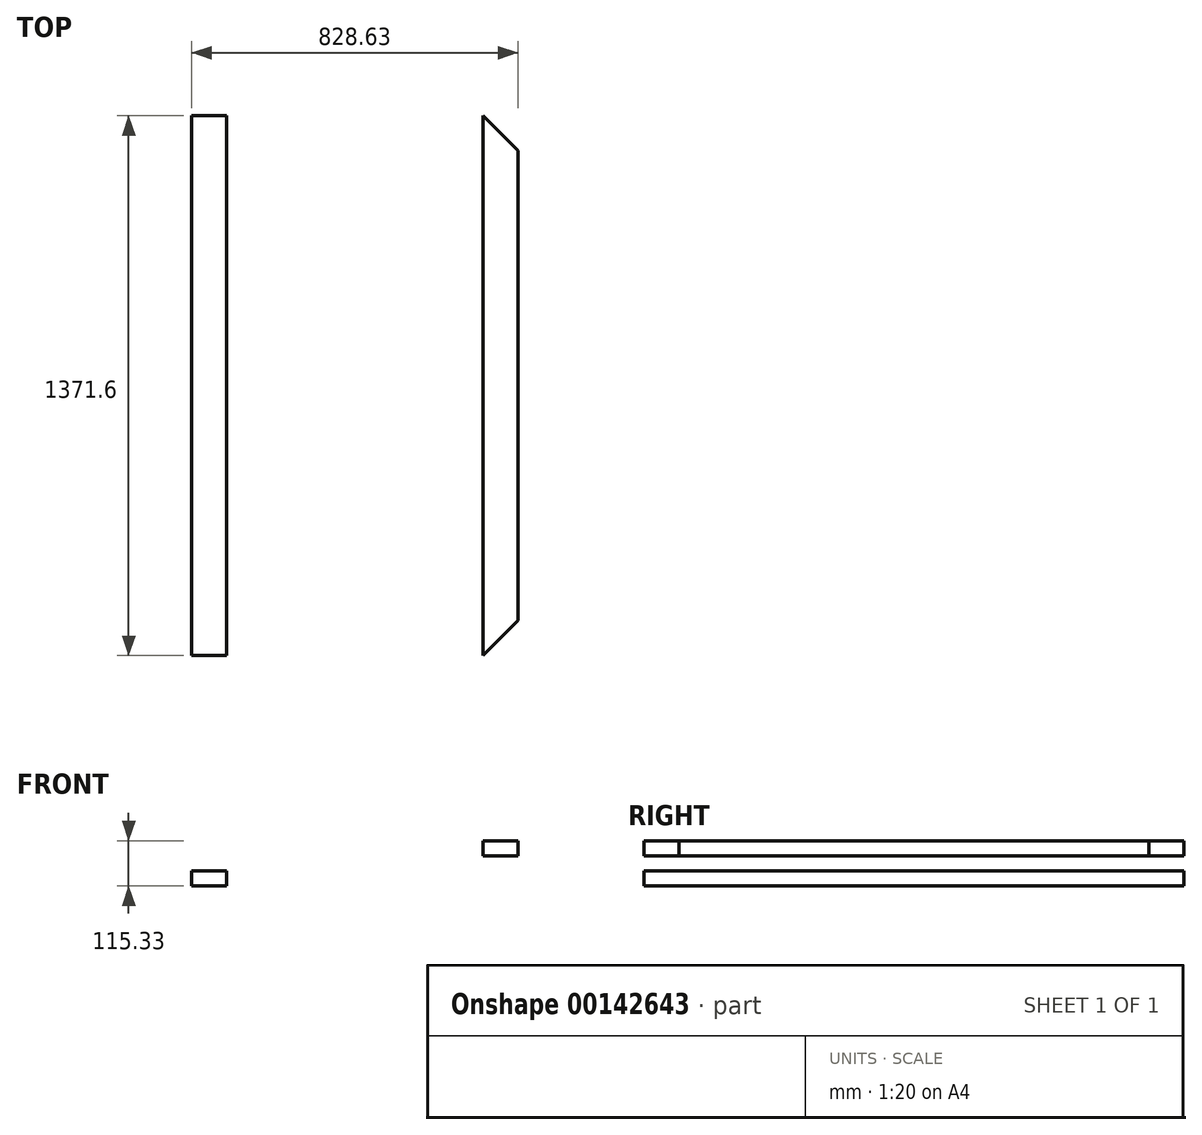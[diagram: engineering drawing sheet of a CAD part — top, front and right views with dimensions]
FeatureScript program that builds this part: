
annotation { "Feature Type Name" : "Feature", "Feature Type Description" : "" }
export const myFeature = defineFeature(function(context is Context, id is Id, definition is map)
    precondition{}
    {
        {
            var Q0;
            Q0=qCreatedBy(makeId("Front.planeOp"),FACE);
            var sketch = newSketch(context, id + "F0", { "sketchPlane" : qUnion([Q0])});
            skLineSegment(sketch, "E0.bottom", {"start": v(0, 0) * mm, "end": v(88.9, 0) * mm});
            skLineSegment(sketch, "E0.top", {"start": v(0, 38.1) * mm, "end": v(88.9, 38.1) * mm});
            skLineSegment(sketch, "E0.left", {"start": v(0, 0) * mm, "end": v(0, 38.1) * mm});
            skLineSegment(sketch, "E0.right", {"start": v(88.9, 0) * mm, "end": v(88.9, 38.1) * mm});
            skSolve(sketch);
        }
        {
            var Q0;
            Q0 = qSketchRegion(id + "F0", true);
            extrude(context, id + "F1", {"entities" : qUnion([Q0]), "depth" : 1371.6 * mm});
        }
        {
            var Q0;
            Q0=makeQuery(id+"F1.opExtrude","SWEPT_FACE",FACE,{"disambiguationData":[OSD([sQuery(id+"F0.wireOp",EDGE,"E0.top")])]});
            var sketch = newSketch(context, id + "F2", { "sketchPlane" : qUnion([Q0])});
            skLineSegment(sketch, "E1", {"start": v(0, -1371.6) * mm, "end": v(88.9, -1282.7) * mm});
            skLineSegment(sketch, "E2", {"start": v(88.9, -1282.7) * mm, "end": v(88.9, -1371.6) * mm});
            skLineSegment(sketch, "E3", {"start": v(88.9, -1371.6) * mm, "end": v(0, -1371.6) * mm});
            skLineSegment(sketch, "E4", {"start": v(88.9, -88.9) * mm, "end": v(0, 0) * mm});
            skLineSegment(sketch, "E5", {"start": v(0, 0) * mm, "end": v(88.9, 0) * mm});
            skLineSegment(sketch, "E6", {"start": v(88.9, 0) * mm, "end": v(88.9, -88.9) * mm});
            skSolve(sketch);
        }
        {
            var Q0;
            Q0 = qSketchRegion(id + "F2", true);
            extrude(context, id + "F3", {"entities" : qUnion([Q0]), "operationType" : NewBodyOperationType.REMOVE, "endBound" : BoundingType.UP_TO_NEXT, "oppositeDirection" : true, "depth" : 25.4 * mm});
        }
        {
            var Q0;
            Q0=qCreatedBy(makeId("Front.planeOp"),FACE);
            var sketch = newSketch(context, id + "F4", { "sketchPlane" : qUnion([Q0])});
            skLineSegment(sketch, "E7.bottom", {"start": v(-739.73, -77.23) * mm, "end": v(-650.83, -77.23) * mm});
            skLineSegment(sketch, "E7.top", {"start": v(-739.73, -39.13) * mm, "end": v(-650.83, -39.13) * mm});
            skLineSegment(sketch, "E7.left", {"start": v(-739.73, -77.23) * mm, "end": v(-739.73, -39.13) * mm});
            skLineSegment(sketch, "E7.right", {"start": v(-650.83, -77.23) * mm, "end": v(-650.83, -39.13) * mm});
            skSolve(sketch);
        }
        {
            var Q0;
            Q0 = qSketchRegion(id + "F4", true);
            extrude(context, id + "F5", {"entities" : qUnion([Q0]), "depth" : 1371.6 * mm});
        }
    });
